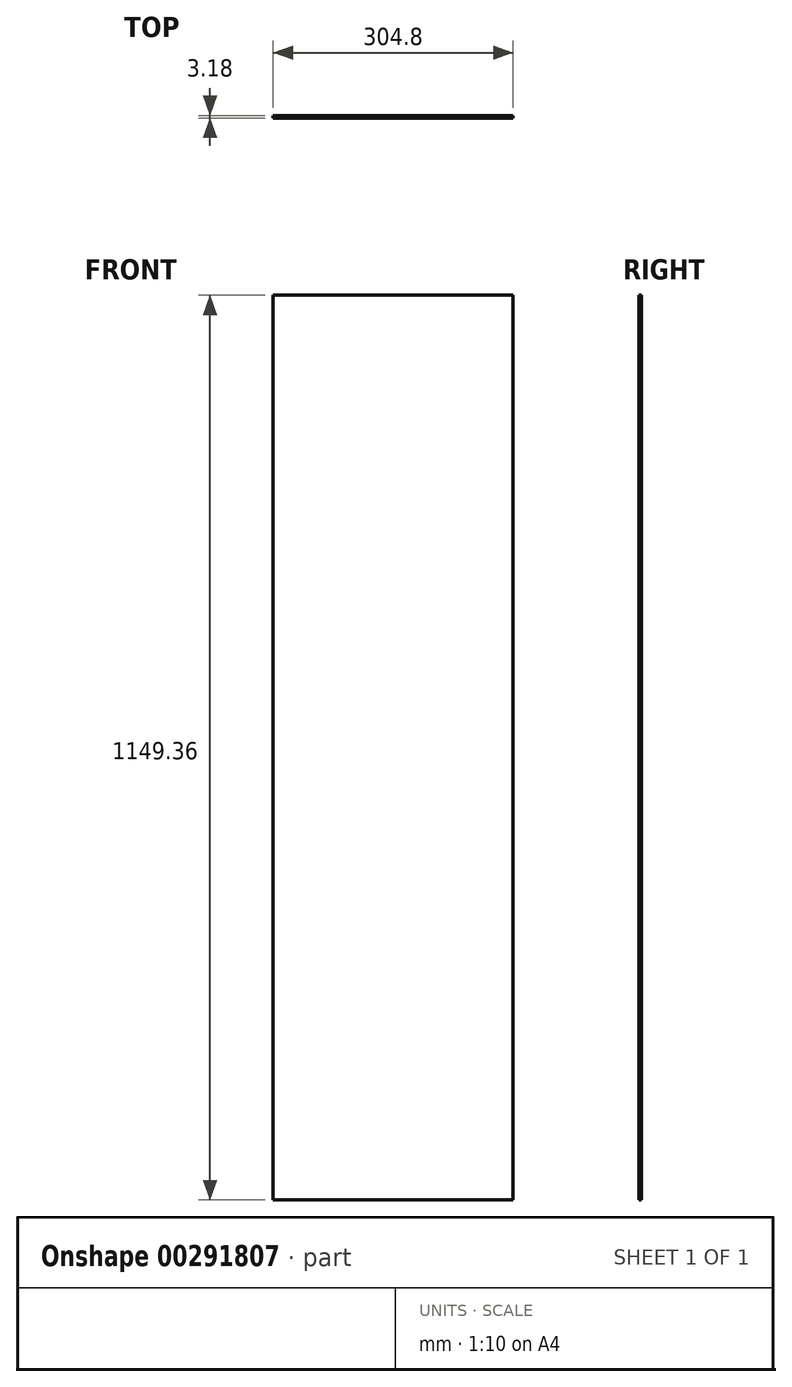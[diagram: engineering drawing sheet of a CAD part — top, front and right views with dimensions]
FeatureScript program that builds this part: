
annotation { "Feature Type Name" : "Feature", "Feature Type Description" : "" }
export const myFeature = defineFeature(function(context is Context, id is Id, definition is map)
    precondition{}
    {
        {
            var Q0;
            Q0=qCreatedBy(makeId("Front.planeOp"),FACE);
            var sketch = newSketch(context, id + "F0", { "sketchPlane" : qUnion([Q0])});
            skLineSegment(sketch, "E0.bottom", {"start": v(152.4, 574.68) * mm, "end": v(-152.4, 574.68) * mm});
            skLineSegment(sketch, "E0.top", {"start": v(152.4, -574.68) * mm, "end": v(-152.4, -574.68) * mm});
            skLineSegment(sketch, "E0.left", {"start": v(152.4, 574.68) * mm, "end": v(152.4, -574.68) * mm});
            skLineSegment(sketch, "E0.right", {"start": v(-152.4, 574.68) * mm, "end": v(-152.4, -574.68) * mm});
            skPoint(sketch, "E0.middle", {"position": v(0, 0) * mm});
            skSolve(sketch);
        }
        {
            var Q0;
            Q0 = qSketchRegion(id + "F0", true);
            extrude(context, id + "F1", {"entities" : qUnion([Q0]), "endBound" : BoundingType.SYMMETRIC, "depth" : 3.17 * mm});
        }
    });
